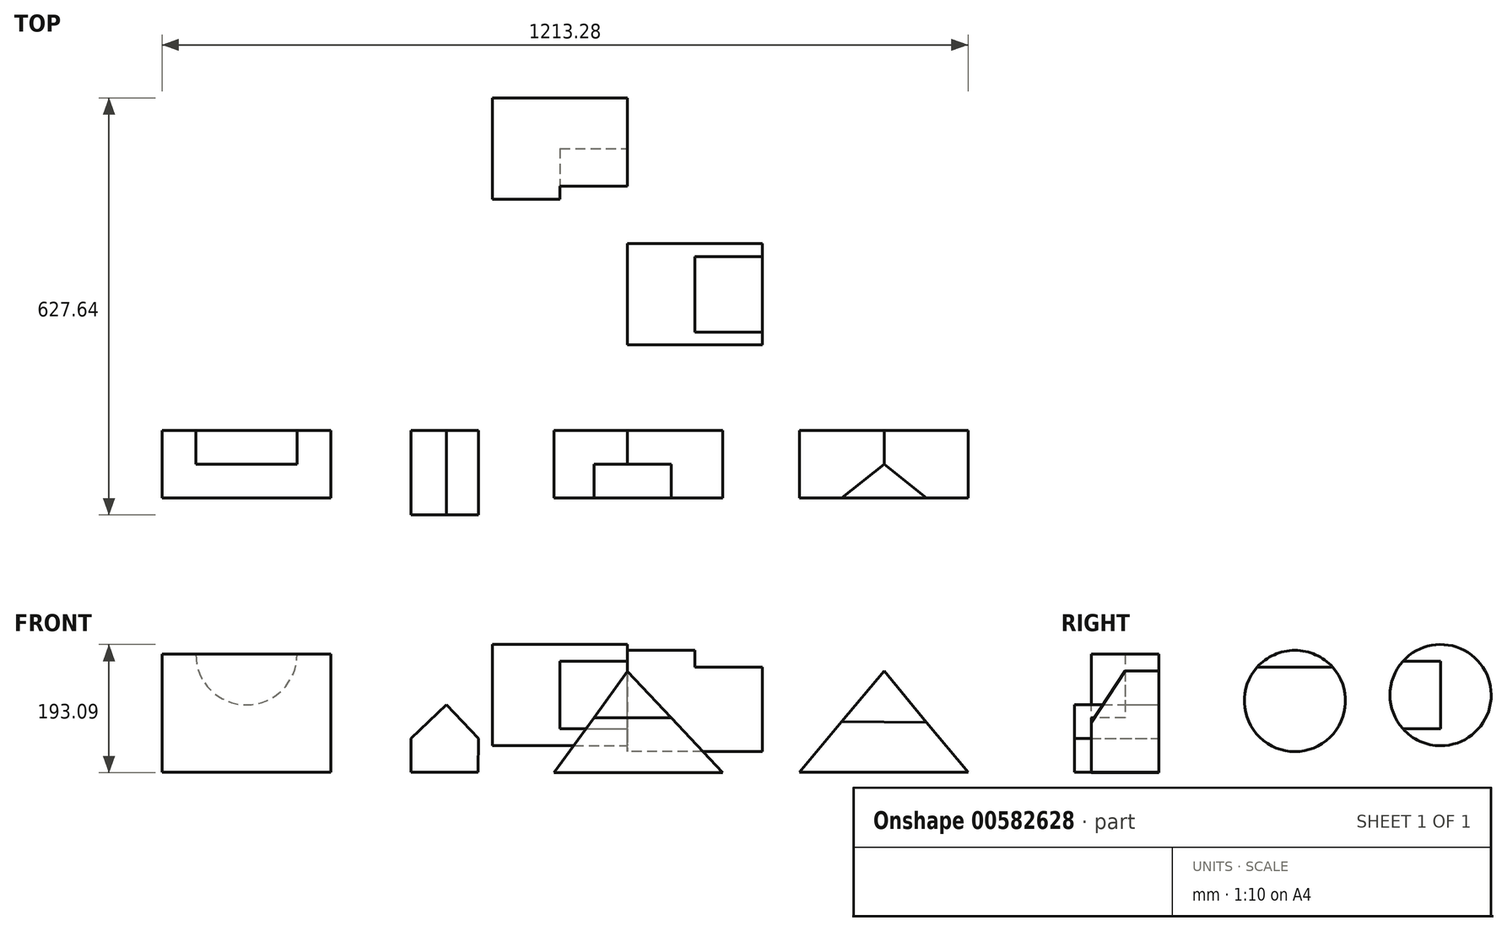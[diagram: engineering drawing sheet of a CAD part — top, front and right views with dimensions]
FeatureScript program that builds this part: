
annotation { "Feature Type Name" : "Feature", "Feature Type Description" : "" }
export const myFeature = defineFeature(function(context is Context, id is Id, definition is map)
    precondition{}
    {
        {
            var Q0;
            Q0=qCreatedBy(makeId("Front.planeOp"),FACE);
            var sketch = newSketch(context, id + "F0", { "sketchPlane" : qUnion([Q0])});
            skLineSegment(sketch, "E0", {"start": v(-110.7, -0.6) * mm, "end": v(143.3, -0.6) * mm});
            skLineSegment(sketch, "E1", {"start": v(143.3, -0.6) * mm, "end": v(0, 151.8) * mm});
            skLineSegment(sketch, "E2", {"start": v(0, 151.8) * mm, "end": v(-110.7, -0.6) * mm});
            skSolve(sketch);
        }
        {
            var Q0;
            Q0=makeQuery(id+"F0.imprint","IMPRINT",FACE,{"disambiguationData":[TD([[makeQuery(id+"F0.imprint","IMPRINT",EDGE,{"derivedFrom":sQuery(id+"F0.wireOp",EDGE,"E0")}),1.0]])]});
            extrude(context, id + "F1", {"entities" : qUnion([Q0]), "depth" : 101.6 * mm, "offsetDistance" : 25.4 * mm});
        }
        {
            var Q0;
            Q0=makeQuery(id+"F1.opExtrude","CAP_FACE",FACE,{"disambiguationData":[OSD([sQuery(id+"F0.wireOp",EDGE,"E0"),sQuery(id+"F0.wireOp",EDGE,"E1"),sQuery(id+"F0.wireOp",EDGE,"E2")])],"isStart":false});
            var sketch = newSketch(context, id + "F2", { "sketchPlane" : qUnion([Q0])});
            skLineSegment(sketch, "E3", {"start": v(0, 81.94) * mm, "end": v(65.7, 81.94) * mm});
            skLineSegment(sketch, "E4", {"start": v(0, 81.94) * mm, "end": v(-50.74, 81.94) * mm});
            skSolve(sketch);
        }
        {
            var Q0;
            {var subQ0=sQuery(id+"F2.wireOp",EDGE,"E3");Q0=makeQuery(id+"F2.imprint","IMPRINT",FACE,{"disambiguationData":[TD([[makeQuery(id+"F2.imprint","IMPRINT",EDGE,{"derivedFrom":subQ0}),1.0]])]});}
            extrude(context, id + "F3", {"entities" : qUnion([Q0]), "operationType" : NewBodyOperationType.REMOVE, "oppositeDirection" : true, "depth" : 50.8 * mm, "offsetDistance" : 25.4 * mm});
        }
        {
            var Q0;
            Q0=qCreatedBy(makeId("Front.planeOp"),FACE);
            var sketch = newSketch(context, id + "F4", { "sketchPlane" : qUnion([Q0])});
            skLineSegment(sketch, "E5", {"start": v(258.53, 0) * mm, "end": v(386.46, 152.4) * mm});
            skLineSegment(sketch, "E6", {"start": v(386.46, 152.4) * mm, "end": v(512.53, 0) * mm});
            skLineSegment(sketch, "E7", {"start": v(512.53, 0) * mm, "end": v(258.53, 0) * mm});
            skSolve(sketch);
        }
        {
            var Q0;
            Q0=makeQuery(id+"F4.imprint","IMPRINT",FACE,{"disambiguationData":[TD([[makeQuery(id+"F4.imprint","IMPRINT",EDGE,{"derivedFrom":sQuery(id+"F4.wireOp",EDGE,"E5")}),-1.0]])]});
            extrude(context, id + "F5", {"entities" : qUnion([Q0]), "depth" : 101.6 * mm, "offsetDistance" : 25.4 * mm});
        }
        {
            var Q0;
            Q0=makeQuery(id+"F5.opExtrude","CAP_EDGE",EDGE,{"disambiguationData":[OSD([sQuery(id+"F4.wireOp",EDGE,"E7")])],"isStart":false});
            cPoint(context, id + "F6", {"entities" : qUnion([Q0]), "parameter" : 0.5});
        }
        {
            var Q0;
            Q0=makeQuery(id+"F5.opExtrude","CAP_VERTEX",VERTEX,{"disambiguationData":[OSD([sQuery(id+"F4.wireOp",EDGE,"E5"),sQuery(id+"F4.wireOp",EDGE,"E6")])],"isStart":false});
            var Q1;
            Q1=makeQuery(id+"F5.opExtrude","CAP_VERTEX",VERTEX,{"disambiguationData":[OSD([sQuery(id+"F4.wireOp",EDGE,"E5"),sQuery(id+"F4.wireOp",EDGE,"E6")])],"isStart":true});
            var Q2;
            Q2 = qCreatedBy(id + "F6" ,VERTEX);
            cPlane(context, id + "F7", {"entities" : qUnion([Q0, Q1, Q2]), "cplaneType" : CPlaneType.THREE_POINT, "offset" : 25.4 * mm, "width" : 152.4 * mm, "height" : 152.4 * mm});
        }
        {
            var Q0;
            Q0=qCreatedBy(id+"F7.planeOp",FACE);
            var sketch = newSketch(context, id + "F8", { "sketchPlane" : qUnion([Q0])});
            skLineSegment(sketch, "E8.0", {"start": v(-101.6, 154.77) * mm, "end": v(0, 154.77) * mm});
            skLineSegment(sketch, "E9.0", {"start": v(0, 151.8) * mm, "end": v(0, -1.28) * mm});
            skLineSegment(sketch, "E10.0", {"start": v(-101.6, 0.28) * mm, "end": v(0, 0.28) * mm});
            skLineSegment(sketch, "E11.0", {"start": v(-101.6, 1.58) * mm, "end": v(-101.6, 154.77) * mm});
            skLineSegment(sketch, "E12", {"start": v(-50.8, 154.77) * mm, "end": v(-101.6, 78.17) * mm});
            skSolve(sketch);
        }
        {
            var Q0;
            {var subQ3=sQuery(id+"F8.wireOp",EDGE,"E12");Q0=makeQuery(id+"F8.imprint","IMPRINT",FACE,{"disambiguationData":[TD([[makeQuery(id+"F8.imprint","IMPRINT",EDGE,{"derivedFrom":subQ3}),-1.0]])]});}
            var Q1;
            Q1=sQuery(id+"F8.wireOp",EDGE,"E12");
            var Q2;
            Q2=sQuery(id+"F8.wireOp",EDGE,"E11.0");
            var Q3;
            Q3=sQuery(id+"F8.wireOp",EDGE,"E8.0");
            extrude(context, id + "F9", {"entities" : qUnion([Q0]), "operationType" : NewBodyOperationType.REMOVE, "surfaceEntities" : qUnion([Q1, Q2, Q3]), "endBound" : BoundingType.SYMMETRIC, "depth" : 355.6 * mm, "offsetDistance" : 25.4 * mm});
        }
        {
            var Q0;
            Q0=qCreatedBy(makeId("Front.planeOp"),FACE);
            var sketch = newSketch(context, id + "F10", { "sketchPlane" : qUnion([Q0])});
            skLineSegment(sketch, "E13", {"start": v(-224.78, 0) * mm, "end": v(-326.38, 0) * mm});
            skLineSegment(sketch, "E14", {"start": v(-326.38, 0) * mm, "end": v(-326.38, 50.8) * mm});
            skLineSegment(sketch, "E15", {"start": v(-326.38, 50.8) * mm, "end": v(-273, 101.6) * mm});
            skLineSegment(sketch, "E16", {"start": v(-273, 101.6) * mm, "end": v(-224.66, 50.8) * mm});
            skLineSegment(sketch, "E17", {"start": v(-224.66, 50.8) * mm, "end": v(-224.78, 0) * mm});
            skSolve(sketch);
        }
        {
            var Q0;
            Q0=makeQuery(id+"F10.imprint","IMPRINT",FACE,{"disambiguationData":[TD([[makeQuery(id+"F10.imprint","IMPRINT",EDGE,{"derivedFrom":sQuery(id+"F10.wireOp",EDGE,"E13")}),-1.0]])]});
            extrude(context, id + "F11", {"entities" : qUnion([Q0]), "depth" : 127 * mm, "offsetDistance" : 25.4 * mm});
        }
        {
            var Q0;
            Q0=makeQuery(id+"F11.opExtrude","CAP_FACE",FACE,{"disambiguationData":[OSD([sQuery(id+"F10.wireOp",EDGE,"E13"),sQuery(id+"F10.wireOp",EDGE,"E14"),sQuery(id+"F10.wireOp",EDGE,"E15"),sQuery(id+"F10.wireOp",EDGE,"E16"),sQuery(id+"F10.wireOp",EDGE,"E17")])],"isStart":false});
            var sketch = newSketch(context, id + "F12", { "sketchPlane" : qUnion([Q0])});
            skLineSegment(sketch, "E18", {"start": v(-273, 101.6) * mm, "end": v(-273, 0) * mm});
            skSolve(sketch);
        }
        {
            var Q0;
            Q0=makeQuery(id+"F11.opExtrude","CAP_VERTEX",VERTEX,{"disambiguationData":[OSD([sQuery(id+"F10.wireOp",EDGE,"E15"),sQuery(id+"F10.wireOp",EDGE,"E16")])],"isStart":true});
            var Q1;
            Q1=sQuery(id+"F12.wireOp",VERTEX,"E18.start");
            var Q2;
            Q2=sQuery(id+"F12.wireOp",VERTEX,"E18.end");
            cPlane(context, id + "F13", {"entities" : qUnion([Q0, Q1, Q2]), "cplaneType" : CPlaneType.THREE_POINT, "offset" : 25.4 * mm, "width" : 152.4 * mm, "height" : 152.4 * mm});
        }
        {
            var Q0;
            Q0=qCreatedBy(id+"F13.planeOp",FACE);
            var sketch = newSketch(context, id + "F14", { "sketchPlane" : qUnion([Q0])});
            skLineSegment(sketch, "E19", {"start": v(84.27, 0) * mm, "end": v(84.27, 50.8) * mm});
            skLineSegment(sketch, "E20", {"start": v(84.27, 50.8) * mm, "end": v(38.1, 88.9) * mm});
            skLineSegment(sketch, "E21", {"start": v(38.1, 88.9) * mm, "end": v(0, 50.8) * mm});
            skLineSegment(sketch, "E22", {"start": v(0, 50.8) * mm, "end": v(0, 0) * mm});
            skLineSegment(sketch, "E23", {"start": v(0, 0) * mm, "end": v(84.27, 0) * mm});
            skSolve(sketch);
        }
        {
            var Q0;
            Q0=sQuery(id+"F14.wireOp",EDGE,"E20");
            var Q1;
            Q1=sQuery(id+"F14.wireOp",EDGE,"E21");
            var Q2;
            Q2=sQuery(id+"F14.wireOp",EDGE,"E22");
            var Q3;
            Q3=sQuery(id+"F14.wireOp",EDGE,"E23");
            var Q4;
            Q4=sQuery(id+"F14.wireOp",EDGE,"E19");
            extrude(context, id + "F15", {"bodyType" : ToolBodyType.SURFACE, "surfaceEntities" : qUnion([Q0, Q1, Q2, Q3, Q4]), "oppositeDirection" : true, "depth" : 177.8 * mm, "offsetDistance" : 25.4 * mm});
        }
        {
            var Q0;
            Q0=qCreatedBy(makeId("Right.planeOp"),FACE);
            var sketch = newSketch(context, id + "F16", { "sketchPlane" : qUnion([Q0])});
            skCircle(sketch, "E24", {"center": v(205.06, 107.51) * mm, "radius": 76.2 * mm});
            skSolve(sketch);
        }
        {
            var Q0;
            Q0=makeQuery(id+"F16.imprint","IMPRINT",FACE,{"disambiguationData":[TD([[makeQuery(id+"F16.imprint","IMPRINT",EDGE,{"derivedFrom":sQuery(id+"F16.wireOp",EDGE,"E24")}),1.0]])]});
            extrude(context, id + "F17", {"entities" : qUnion([Q0]), "depth" : 203.2 * mm, "offsetDistance" : 25.4 * mm});
        }
        {
            var Q0;
            Q0=makeQuery(id+"F17.opExtrude","CAP_FACE",FACE,{"disambiguationData":[OSD([sQuery(id+"F16.wireOp",EDGE,"E24")])],"isStart":false});
            var sketch = newSketch(context, id + "F18", { "sketchPlane" : qUnion([Q0])});
            skLineSegment(sketch, "E25", {"start": v(148.27, 158.31) * mm, "end": v(261.86, 158.31) * mm});
            skLineSegment(sketch, "E26", {"start": v(261.86, 158.31) * mm, "end": v(205.06, 158.31) * mm});
            skLineSegment(sketch, "E27", {"start": v(205.06, 158.31) * mm, "end": v(205.06, 183.71) * mm});
            skSolve(sketch);
        }
        {
            var Q0;
            Q0 = qSketchRegion(id + "F18", true);
            var Q1;
            {var subQ0=sQuery(id+"F18.wireOp",EDGE,"E25");Q1=makeQuery(id+"F18.imprint","IMPRINT",FACE,{"disambiguationData":[TD([[makeQuery(id+"F18.imprint","IMPRINT",EDGE,{"derivedFrom":subQ0}),1.0]])]});}
            var Q2;
            {var subQ0=sQuery(id+"F18.wireOp",EDGE,"E26");Q2=makeQuery(id+"F18.imprint","IMPRINT",FACE,{"disambiguationData":[TD([[makeQuery(id+"F18.imprint","IMPRINT",EDGE,{"derivedFrom":subQ0}),-1.0]])]});}
            extrude(context, id + "F19", {"entities" : qUnion([Q0, Q1, Q2]), "operationType" : NewBodyOperationType.REMOVE, "oppositeDirection" : true, "depth" : 101.6 * mm, "offsetDistance" : 25.4 * mm});
        }
        {
            var Q0;
            Q0=qCreatedBy(makeId("Right.planeOp"),FACE);
            var sketch = newSketch(context, id + "F20", { "sketchPlane" : qUnion([Q0])});
            skCircle(sketch, "E28", {"center": v(424.44, 116.3) * mm, "radius": 76.2 * mm});
            skSolve(sketch);
        }
        {
            var Q0;
            Q0=makeQuery(id+"F20.imprint","IMPRINT",FACE,{"disambiguationData":[TD([[makeQuery(id+"F20.imprint","IMPRINT",EDGE,{"derivedFrom":sQuery(id+"F20.wireOp",EDGE,"E28")}),1.0]])]});
            extrude(context, id + "F21", {"entities" : qUnion([Q0]), "oppositeDirection" : true, "depth" : 203.2 * mm, "offsetDistance" : 25.4 * mm});
        }
        {
            var Q0;
            Q0=makeQuery(id+"F21.opExtrude","CAP_FACE",FACE,{"disambiguationData":[OSD([sQuery(id+"F20.wireOp",EDGE,"E28")])],"isStart":true});
            var sketch = newSketch(context, id + "F22", { "sketchPlane" : qUnion([Q0])});
            skLineSegment(sketch, "E29", {"start": v(424.44, 116.3) * mm, "end": v(424.44, 167.1) * mm});
            skLineSegment(sketch, "E30", {"start": v(424.44, 167.1) * mm, "end": v(367.64, 167.1) * mm});
            skLineSegment(sketch, "E31", {"start": v(367.64, 167.1) * mm, "end": v(424.44, 167.1) * mm});
            skLineSegment(sketch, "E32", {"start": v(424.44, 116.3) * mm, "end": v(424.44, 65.5) * mm});
            skLineSegment(sketch, "E33", {"start": v(424.44, 65.5) * mm, "end": v(367.64, 65.5) * mm});
            skSolve(sketch);
        }
        {
            var Q0;
            Q0=makeQuery(id+"F22.imprint","IMPRINT",FACE,{"disambiguationData":[TD([[makeQuery(id+"F22.imprint","IMPRINT",EDGE,{"derivedFrom":sQuery(id+"F22.wireOp",EDGE,"E29")}),1.0]])]});
            extrude(context, id + "F23", {"entities" : qUnion([Q0]), "operationType" : NewBodyOperationType.REMOVE, "oppositeDirection" : true, "depth" : 101.6 * mm, "offsetDistance" : 25.4 * mm});
        }
        {
            var Q0;
            Q0=qCreatedBy(makeId("Front.planeOp"),FACE);
            var sketch = newSketch(context, id + "F24", { "sketchPlane" : qUnion([Q0])});
            skLineSegment(sketch, "E34", {"start": v(-446.75, 0) * mm, "end": v(-700.75, 0) * mm});
            skLineSegment(sketch, "E35", {"start": v(-700.75, 0) * mm, "end": v(-700.75, 177.8) * mm});
            skLineSegment(sketch, "E36", {"start": v(-700.75, 177.8) * mm, "end": v(-446.75, 177.8) * mm});
            skLineSegment(sketch, "E37", {"start": v(-446.75, 177.8) * mm, "end": v(-446.75, 0) * mm});
            skArc(sketch, "E38", {"start": v(-649.95, 177.8) * mm, "mid": v(-573.75, 101.6) * mm, "end": v(-497.55, 177.8) * mm});
            skSolve(sketch);
        }
        {
            var Q0;
            Q0=makeQuery(id+"F24.imprint","IMPRINT",FACE,{"disambiguationData":[TD([[makeQuery(id+"F24.imprint","IMPRINT",EDGE,{"derivedFrom":sQuery(id+"F24.wireOp",EDGE,"E34")}),-1.0]])]});
            extrude(context, id + "F25", {"entities" : qUnion([Q0]), "depth" : 101.6 * mm, "offsetDistance" : 25.4 * mm});
        }
        {
            var Q0;
            Q0=makeQuery(id+"F25.opExtrude","CAP_FACE",FACE,{"disambiguationData":[OSD([sQuery(id+"F24.wireOp",EDGE,"E34"),sQuery(id+"F24.wireOp",EDGE,"E35"),sQuery(id+"F24.wireOp",EDGE,"E36"),sQuery(id+"F24.wireOp",EDGE,"E37"),sQuery(id+"F24.wireOp",EDGE,"E38")])],"isStart":false});
            var sketch = newSketch(context, id + "F26", { "sketchPlane" : qUnion([Q0])});
            skLineSegment(sketch, "E39", {"start": v(-497.55, 177.8) * mm, "end": v(-649.95, 177.8) * mm});
            skSolve(sketch);
        }
        {
            var Q0;
            Q0=makeQuery(id+"F26.imprint","IMPRINT",FACE,{"disambiguationData":[TD([[makeQuery(id+"F26.imprint","IMPRINT",EDGE,{"derivedFrom":sQuery(id+"F26.wireOp",EDGE,"E39")}),1.0]])]});
            extrude(context, id + "F27", {"entities" : qUnion([Q0]), "operationType" : NewBodyOperationType.ADD, "oppositeDirection" : true, "depth" : 50.8 * mm, "offsetDistance" : 25.4 * mm});
        }
    });
